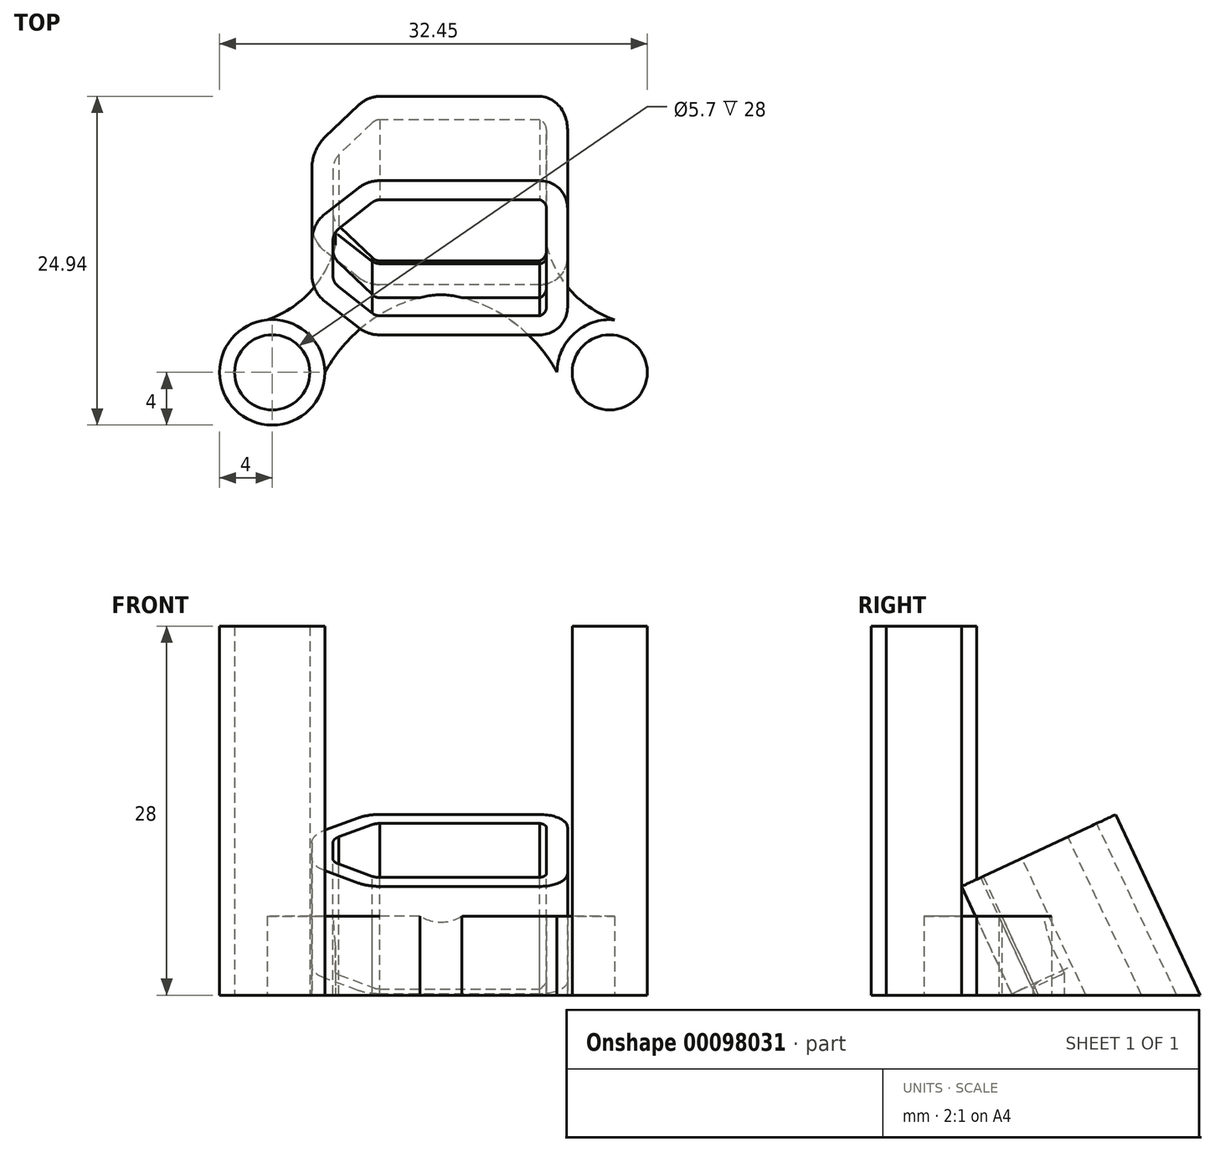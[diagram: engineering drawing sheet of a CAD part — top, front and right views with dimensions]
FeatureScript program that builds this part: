
annotation { "Feature Type Name" : "Feature", "Feature Type Description" : "" }
export const myFeature = defineFeature(function(context is Context, id is Id, definition is map)
    precondition{}
    {
        {
            var Q0;
            Q0=qCreatedBy(makeId("Top.planeOp"),FACE);
            var sketch = newSketch(context, id + "F0", { "sketchPlane" : qUnion([Q0])});
            skLineSegment(sketch, "E0", {"start": v(0, 0) * mm, "end": v(-12.8, 0) * mm, "construction": true});
            skCircle(sketch, "E1", {"center": v(-12.8, 0) * mm, "radius": 2.85 * mm});
            skCircle(sketch, "E2", {"center": v(-12.8, 0) * mm, "radius": 4 * mm});
            skCircle(sketch, "E3.MirrorC", {"center": v(12.8, 0) * mm, "radius": 2.85 * mm});
            skCircle(sketch, "E4.MirrorC", {"center": v(12.8, 0) * mm, "radius": 4 * mm});
            skSolve(sketch);
        }
        {
            var Q0;
            Q0=qCreatedBy(makeId("Top.planeOp"),FACE);
            var sketch = newSketch(context, id + "F1", { "sketchPlane" : qUnion([Q0])});
            skCircle(sketch, "E5", {"center": v(0, 0) * mm, "radius": 5.89 * mm});
            skLineSegment(sketch, "E6", {"start": v(0, 0) * mm, "end": v(0, 12.5) * mm, "construction": true});
            skLineSegment(sketch, "E7", {"start": v(0, 12.5) * mm, "end": v(8, 12.5) * mm, "construction": true});
            skLineSegment(sketch, "E8", {"start": v(0, 12.5) * mm, "end": v(-8.2, 12.5) * mm, "construction": true});
            skLineSegment(sketch, "E9", {"start": v(0, 12.5) * mm, "end": v(0, 16.75) * mm, "construction": true});
            skLineSegment(sketch, "E10", {"start": v(8, 12.5) * mm, "end": v(8, 16.25) * mm});
            skLineSegment(sketch, "E11", {"start": v(-4.66, 16.75) * mm, "end": v(7.5, 16.75) * mm});
            skLineSegment(sketch, "E12", {"start": v(-8.2, 12.5) * mm, "end": v(-8.2, 13.76) * mm});
            skLineSegment(sketch, "E13", {"start": v(-7.82, 14.55) * mm, "end": v(-5.27, 16.54) * mm});
            skLineSegment(sketch, "E14.MirrorCS", {"start": v(-4.66, 8.25) * mm, "end": v(7.5, 8.25) * mm});
            skLineSegment(sketch, "E15.MirrorCS", {"start": v(8, 12.5) * mm, "end": v(8, 8.75) * mm});
            skLineSegment(sketch, "E16.MirrorCS", {"start": v(-8.2, 12.5) * mm, "end": v(-8.2, 11.24) * mm});
            skLineSegment(sketch, "E17.MirrorCS", {"start": v(-7.82, 10.45) * mm, "end": v(-5.27, 8.46) * mm});
            skPoint(sketch, "E18.visualSharp", {"position": v(-8.2, 14.25) * mm});
            skArc(sketch, "E18.filletArc", {"start": v(-7.82, 14.55) * mm, "mid": v(-8.1, 14.2) * mm, "end": v(-8.2, 13.76) * mm});
            skPoint(sketch, "E19.visualSharp", {"position": v(-5, 16.75) * mm});
            skArc(sketch, "E19.filletArc", {"start": v(-4.66, 16.75) * mm, "mid": v(-4.98, 16.7) * mm, "end": v(-5.27, 16.54) * mm});
            skPoint(sketch, "E20.visualSharp", {"position": v(-8.2, 10.75) * mm});
            skArc(sketch, "E20.filletArc", {"start": v(-8.2, 11.24) * mm, "mid": v(-8.1, 10.8) * mm, "end": v(-7.82, 10.45) * mm});
            skPoint(sketch, "E21.visualSharp", {"position": v(-5, 8.25) * mm});
            skArc(sketch, "E21.filletArc", {"start": v(-5.27, 8.46) * mm, "mid": v(-4.98, 8.3) * mm, "end": v(-4.66, 8.25) * mm});
            skPoint(sketch, "E22.visualSharp", {"position": v(8, 8.25) * mm});
            skArc(sketch, "E22.filletArc", {"start": v(7.5, 8.25) * mm, "mid": v(7.85, 8.4) * mm, "end": v(8, 8.75) * mm});
            skPoint(sketch, "E23.visualSharp", {"position": v(8, 16.75) * mm});
            skArc(sketch, "E23.filletArc", {"start": v(8, 16.25) * mm, "mid": v(7.85, 16.6) * mm, "end": v(7.5, 16.75) * mm});
            skLineSegment(sketch, "E24", {"start": v(0, 0) * mm, "end": v(-12.8, 0) * mm, "construction": true});
            skCircle(sketch, "E25", {"center": v(-12.8, 0) * mm, "radius": 4 * mm});
            skCircle(sketch, "E26.MirrorC", {"center": v(12.8, 0) * mm, "radius": 4 * mm});
            skArc(sketch, "E27", {"start": v(8, 9.68) * mm, "mid": v(10.32, 5.71) * mm, "end": v(14.43, 3.65) * mm});
            skArc(sketch, "E28.MirrorCS", {"start": v(-8, 9.68) * mm, "mid": v(-10.32, 5.71) * mm, "end": v(-14.43, 3.65) * mm});
            skLineSegment(sketch, "E29", {"start": v(-8, 9.68) * mm, "end": v(-8, 10.64) * mm});
            skArc(sketch, "E30", {"start": v(-1.26, 5.75) * mm, "mid": v(-5.65, 3.68) * mm, "end": v(-8.8, 0) * mm});
            skArc(sketch, "E31.MirrorCS", {"start": v(1.26, 5.75) * mm, "mid": v(5.65, 3.68) * mm, "end": v(8.8, 0) * mm});
            skSolve(sketch);
        }
        {
            var Q0;
            Q0=makeQuery(id+"F0.imprint","IMPRINT",FACE,{"disambiguationData":[TD([[makeQuery(id+"F0.imprint","IMPRINT",EDGE,{"derivedFrom":sQuery(id+"F0.wireOp",EDGE,"E1")}),-1.0]])]});
            var Q1;
            Q1=makeQuery(id+"F0.imprint","IMPRINT",FACE,{"disambiguationData":[TD([[makeQuery(id+"F0.imprint","IMPRINT",EDGE,{"derivedFrom":sQuery(id+"F0.wireOp",EDGE,"E3.MirrorC")}),1.0]])]});
            extrude(context, id + "F2", {"entities" : qUnion([Q0, Q1]), "depth" : 28 * mm});
        }
        {
            var Q0;
            Q0=qCreatedBy(makeId("Top.planeOp"),FACE);
            var sketch = newSketch(context, id + "F3", { "sketchPlane" : qUnion([Q0])});
            skLineSegment(sketch, "E32.0", {"start": v(-4.66, 18.35) * mm, "end": v(7.5, 18.35) * mm});
            skLineSegment(sketch, "E33.0", {"start": v(9.6, 12.5) * mm, "end": v(9.6, 16.25) * mm});
            skLineSegment(sketch, "E34.0", {"start": v(-8.8, 15.81) * mm, "end": v(-6.26, 17.8) * mm});
            skLineSegment(sketch, "E35.0", {"start": v(-9.8, 12.5) * mm, "end": v(-9.8, 13.76) * mm});
            skArc(sketch, "E36", {"start": v(-8.8, 15.81) * mm, "mid": v(-9.54, 14.9) * mm, "end": v(-9.8, 13.76) * mm});
            skArc(sketch, "E37", {"start": v(-4.66, 18.35) * mm, "mid": v(-5.5, 18.2) * mm, "end": v(-6.26, 17.8) * mm});
            skArc(sketch, "E38", {"start": v(9.6, 16.25) * mm, "mid": v(8.98, 17.73) * mm, "end": v(7.5, 18.35) * mm});
            skLineSegment(sketch, "E39.0", {"start": v(-8.8, 9.19) * mm, "end": v(-6.26, 7.2) * mm});
            skLineSegment(sketch, "E40.0", {"start": v(-4.66, 6.65) * mm, "end": v(7.5, 6.65) * mm});
            skLineSegment(sketch, "E41.0", {"start": v(9.6, 12.5) * mm, "end": v(9.6, 8.75) * mm});
            skLineSegment(sketch, "E42.0", {"start": v(-9.8, 12.5) * mm, "end": v(-9.8, 11.24) * mm});
            skArc(sketch, "E43.MirrorCS", {"start": v(-8.8, 9.19) * mm, "mid": v(-9.54, 10.1) * mm, "end": v(-9.8, 11.24) * mm});
            skArc(sketch, "E44.MirrorCS", {"start": v(-4.66, 6.65) * mm, "mid": v(-5.5, 6.8) * mm, "end": v(-6.26, 7.2) * mm});
            skArc(sketch, "E45.MirrorCS", {"start": v(9.6, 8.75) * mm, "mid": v(8.98, 7.27) * mm, "end": v(7.5, 6.65) * mm});
            skSolve(sketch);
        }
        {
            var Q0;
            Q0=makeQuery(id+"F3.imprint","IMPRINT",FACE,{"disambiguationData":[TD([[makeQuery(id+"F3.imprint","IMPRINT",EDGE,{"derivedFrom":sQuery(id+"F3.wireOp",EDGE,"E32.0")}),-1.0]])]});
            extrude(context, id + "F4", {"entities" : qUnion([Q0]), "depth" : 6 * mm});
        }
        {
            var Q0;
            Q0=qCreatedBy(makeId("Right.planeOp"),FACE);
            cPlane(context, id + "F5", {"entities" : qUnion([Q0]), "cplaneType" : CPlaneType.OFFSET, "offset" : 9.6 * mm, "width" : 150 * mm, "height" : 150 * mm});
        }
        {
            var Q0;
            Q0=qCreatedBy(id+"F5.planeOp",FACE);
            var sketch = newSketch(context, id + "F6", { "sketchPlane" : qUnion([Q0])});
            skLineSegment(sketch, "E46", {"start": v(6.45, 0) * mm, "end": v(21.04, 6.8) * mm});
            skLineSegment(sketch, "E47", {"start": v(6.45, 0) * mm, "end": v(6.45, 6.8) * mm});
            skLineSegment(sketch, "E48", {"start": v(6.45, 6.8) * mm, "end": v(21.04, 6.8) * mm});
            skSolve(sketch);
        }
        {
            var Q0;
            Q0=makeQuery(id+"F6.imprint","IMPRINT",FACE,{"disambiguationData":[TD([[makeQuery(id+"F6.imprint","IMPRINT",EDGE,{"derivedFrom":sQuery(id+"F6.wireOp",EDGE,"s5qhwvRX-1pLo-hh37-W3cO-p8a1964w9mC2")}),-1.0]])]});
            var Q1;
            Q1=makeQuery(id+"F6.imprint","IMPRINT",FACE,{"disambiguationData":[TD([[makeQuery(id+"F6.imprint","IMPRINT",EDGE,{"derivedFrom":sQuery(id+"F6.wireOp",EDGE,"E46")}),1.0]])]});
            extrude(context, id + "F7", {"entities" : qUnion([Q0, Q1]), "operationType" : NewBodyOperationType.REMOVE, "oppositeDirection" : true, "depth" : 50 * mm});
        }
        {
            var Q0;
            Q0=makeQuery(id+"F7.boolean.opBoolean","COPY",FACE,{"derivedFrom":makeQuery(id+"F7.opExtrude","SWEPT_FACE",FACE,{"disambiguationData":[OSD([sQuery(id+"F6.wireOp",EDGE,"E46")])]})});
            var Q1;
            Q1=makeQuery(id+"F4.opExtrude","CAP_FACE",FACE,{"disambiguationData":[OSD([sQuery(id+"F3.wireOp",EDGE,"E32.0"),sQuery(id+"F3.wireOp",EDGE,"E33.0"),sQuery(id+"F3.wireOp",EDGE,"E34.0"),sQuery(id+"F3.wireOp",EDGE,"E35.0"),sQuery(id+"F3.wireOp",EDGE,"E36"),sQuery(id+"F3.wireOp",EDGE,"E37"),sQuery(id+"F3.wireOp",EDGE,"E38"),sQuery(id+"F3.wireOp",EDGE,"E39.0"),sQuery(id+"F3.wireOp",EDGE,"E40.0"),sQuery(id+"F3.wireOp",EDGE,"E41.0"),sQuery(id+"F3.wireOp",EDGE,"E42.0"),sQuery(id+"F3.wireOp",EDGE,"E43.MirrorCS"),sQuery(id+"F3.wireOp",EDGE,"E44.MirrorCS"),sQuery(id+"F3.wireOp",EDGE,"E45.MirrorCS")])],"isStart":true});
            extrude(context, id + "F8", {"entities" : qUnion([Q0]), "operationType" : NewBodyOperationType.ADD, "endBound" : BoundingType.UP_TO_SURFACE, "oppositeDirection" : true, "endBoundEntityFace" : qUnion([Q1]), "depth" : 25 * mm});
        }
        {
            var Q0;
            Q0=makeQuery(id+"F7.boolean.opBoolean","COPY",FACE,{"derivedFrom":makeQuery(id+"F7.opExtrude","SWEPT_FACE",FACE,{"disambiguationData":[OSD([sQuery(id+"F6.wireOp",EDGE,"E46")])]})});
            extrude(context, id + "F9", {"entities" : qUnion([Q0]), "operationType" : NewBodyOperationType.ADD, "depth" : 9 * mm});
        }
        {
            var Q0;
            Q0=makeQuery(id+"F1.imprint","IMPRINT",FACE,{"disambiguationData":[TD([[makeQuery(id+"F1.imprint","IMPRINT",EDGE,{"derivedFrom":sQuery(id+"F1.wireOp",EDGE,"E14.MirrorCS")}),-1.0]])]});
            extrude(context, id + "F10", {"entities" : qUnion([Q0]), "depth" : 6 * mm});
        }
        {
            var Q0;
            Q0=makeQuery(id+"F9.opExtrude","CAP_FACE",FACE,{"disambiguationData":[OSD([sQuery(id+"F6.wireOp",EDGE,"E46")])],"isStart":false});
            var sketch = newSketch(context, id + "F11", { "sketchPlane" : qUnion([Q0])});
            skLineSegment(sketch, "E49.0", {"start": v(7.5, 17.38) * mm, "end": v(-4.66, 17.38) * mm});
            skLineSegment(sketch, "E50.0", {"start": v(7.5, 7.67) * mm, "end": v(-4.66, 7.67) * mm});
            skLineSegment(sketch, "E51.0", {"start": v(8, 8.38) * mm, "end": v(8, 16.66) * mm});
            skLineSegment(sketch, "E52.0", {"start": v(-8.2, 13.91) * mm, "end": v(-8.2, 11.13) * mm});
            skLineSegment(sketch, "E53.0", {"start": v(-5.21, 17.16) * mm, "end": v(-7.76, 14.96) * mm});
            skLineSegment(sketch, "E54.0", {"start": v(-5.21, 7.89) * mm, "end": v(-7.76, 10.08) * mm});
            skArc(sketch, "E55", {"start": v(-4.66, 17.38) * mm, "mid": v(-4.95, 17.31) * mm, "end": v(-5.21, 17.16) * mm});
            skArc(sketch, "E56", {"start": v(-7.76, 14.96) * mm, "mid": v(-8.08, 14.48) * mm, "end": v(-8.2, 13.91) * mm});
            skArc(sketch, "E57", {"start": v(-8.2, 11.13) * mm, "mid": v(-8.1, 10.55) * mm, "end": v(-7.76, 10.08) * mm});
            skArc(sketch, "E58", {"start": v(-5.21, 7.89) * mm, "mid": v(-4.95, 7.72) * mm, "end": v(-4.66, 7.67) * mm});
            skArc(sketch, "E59", {"start": v(7.5, 7.67) * mm, "mid": v(7.86, 7.95) * mm, "end": v(8, 8.38) * mm});
            skArc(sketch, "E60", {"start": v(8, 16.66) * mm, "mid": v(7.86, 17.1) * mm, "end": v(7.5, 17.38) * mm});
            skSolve(sketch);
        }
        {
            var Q0;
            Q0=makeQuery(id+"F11.imprint","IMPRINT",FACE,{"disambiguationData":[TD([[makeQuery(id+"F11.imprint","IMPRINT",EDGE,{"derivedFrom":sQuery(id+"F11.wireOp",EDGE,"E49.0")}),1.0]])]});
            extrude(context, id + "F12", {"entities" : qUnion([Q0]), "operationType" : NewBodyOperationType.REMOVE, "oppositeDirection" : true, "depth" : 50 * mm});
        }
    });
